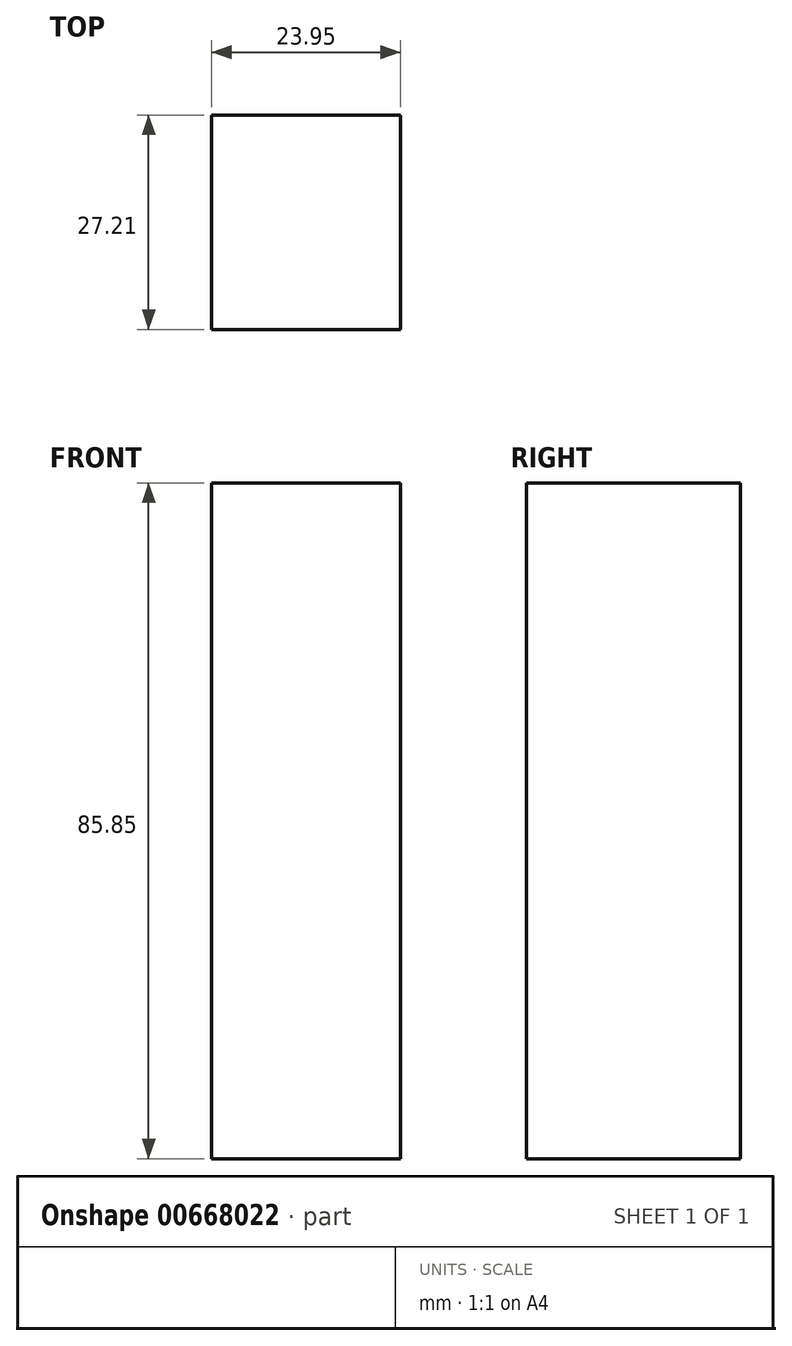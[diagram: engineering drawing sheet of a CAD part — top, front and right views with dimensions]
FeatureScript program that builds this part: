
annotation { "Feature Type Name" : "Feature", "Feature Type Description" : "" }
export const myFeature = defineFeature(function(context is Context, id is Id, definition is map)
    precondition{}
    {
        {
            var Q0;
            Q0=qCreatedBy(makeId("Top.planeOp"),FACE);
            var sketch = newSketch(context, id + "F0", { "sketchPlane" : qUnion([Q0])});
            skLineSegment(sketch, "E0.bottom", {"start": v(-65.47, 56.4) * mm, "end": v(-51.52, 56.4) * mm});
            skLineSegment(sketch, "E0.top", {"start": v(-65.47, -55.94) * mm, "end": v(-51.52, -55.94) * mm});
            skLineSegment(sketch, "E0.left", {"start": v(-65.47, 56.4) * mm, "end": v(-65.47, -55.94) * mm});
            skLineSegment(sketch, "E0.right", {"start": v(-51.52, 56.4) * mm, "end": v(-51.52, -55.94) * mm});
            skLineSegment(sketch, "E1.bottom", {"start": v(-51.52, -42.91) * mm, "end": v(49.42, -42.91) * mm});
            skLineSegment(sketch, "E1.top", {"start": v(-51.52, -55.94) * mm, "end": v(49.42, -55.94) * mm});
            skLineSegment(sketch, "E1.left", {"start": v(-51.52, -42.91) * mm, "end": v(-51.52, -55.94) * mm});
            skLineSegment(sketch, "E1.right", {"start": v(49.42, -42.91) * mm, "end": v(49.42, -55.94) * mm});
            skLineSegment(sketch, "E2.bottom", {"start": v(49.42, -42.91) * mm, "end": v(33.14, -42.91) * mm});
            skLineSegment(sketch, "E2.top", {"start": v(49.42, 55.94) * mm, "end": v(33.14, 55.94) * mm});
            skLineSegment(sketch, "E2.left", {"start": v(49.42, -42.91) * mm, "end": v(49.42, 55.94) * mm});
            skLineSegment(sketch, "E2.right", {"start": v(33.14, -42.91) * mm, "end": v(33.14, 55.94) * mm});
            skLineSegment(sketch, "E3.bottom", {"start": v(33.14, 55.94) * mm, "end": v(-51.52, 55.94) * mm});
            skLineSegment(sketch, "E3.top", {"start": v(33.14, 41.98) * mm, "end": v(-51.52, 41.98) * mm});
            skLineSegment(sketch, "E3.left", {"start": v(33.14, 55.94) * mm, "end": v(33.14, 41.98) * mm});
            skLineSegment(sketch, "E3.right", {"start": v(-51.52, 55.94) * mm, "end": v(-51.52, 41.98) * mm});
            skLineSegment(sketch, "E4.bottom", {"start": v(-44.54, 33.14) * mm, "end": v(-33.14, 33.14) * mm});
            skLineSegment(sketch, "E4.top", {"start": v(-44.54, -37.1) * mm, "end": v(-33.14, -37.1) * mm});
            skLineSegment(sketch, "E4.left", {"start": v(-44.54, 33.14) * mm, "end": v(-44.54, -37.1) * mm});
            skLineSegment(sketch, "E4.right", {"start": v(-33.14, 33.14) * mm, "end": v(-33.14, -37.1) * mm});
            skLineSegment(sketch, "E5.bottom", {"start": v(-33.14, 33.14) * mm, "end": v(25, 33.14) * mm});
            skLineSegment(sketch, "E5.top", {"start": v(-33.14, 24.54) * mm, "end": v(25, 24.54) * mm});
            skLineSegment(sketch, "E5.left", {"start": v(-33.14, 33.14) * mm, "end": v(-33.14, 24.54) * mm});
            skLineSegment(sketch, "E5.right", {"start": v(25, 33.14) * mm, "end": v(25, 24.54) * mm});
            skLineSegment(sketch, "E6.bottom", {"start": v(25, 24.54) * mm, "end": v(17.1, 24.54) * mm});
            skLineSegment(sketch, "E6.top", {"start": v(25, -37.1) * mm, "end": v(17.1, -37.1) * mm});
            skLineSegment(sketch, "E6.left", {"start": v(25, 24.54) * mm, "end": v(25, -37.1) * mm});
            skLineSegment(sketch, "E6.right", {"start": v(17.1, 24.54) * mm, "end": v(17.1, -37.1) * mm});
            skLineSegment(sketch, "E7.bottom", {"start": v(17.1, -29.89) * mm, "end": v(-33.14, -29.89) * mm});
            skLineSegment(sketch, "E7.top", {"start": v(17.1, -37.1) * mm, "end": v(-33.14, -37.1) * mm});
            skLineSegment(sketch, "E7.left", {"start": v(17.1, -29.89) * mm, "end": v(17.1, -37.1) * mm});
            skLineSegment(sketch, "E7.right", {"start": v(-33.14, -29.89) * mm, "end": v(-33.14, -37.1) * mm});
            skLineSegment(sketch, "E8.bottom", {"start": v(-22.21, 11.28) * mm, "end": v(-28.5, 11.28) * mm});
            skLineSegment(sketch, "E8.top", {"start": v(-22.21, -21.98) * mm, "end": v(-28.5, -21.98) * mm});
            skLineSegment(sketch, "E8.left", {"start": v(-22.21, 11.28) * mm, "end": v(-22.21, -21.98) * mm});
            skLineSegment(sketch, "E8.right", {"start": v(-28.5, 11.28) * mm, "end": v(-28.5, -21.98) * mm});
            skLineSegment(sketch, "E9.bottom", {"start": v(-22.21, -21.98) * mm, "end": v(9.42, -21.98) * mm});
            skLineSegment(sketch, "E9.top", {"start": v(-22.21, -15.93) * mm, "end": v(9.42, -15.93) * mm});
            skLineSegment(sketch, "E9.left", {"start": v(-22.21, -21.98) * mm, "end": v(-22.21, -15.93) * mm});
            skLineSegment(sketch, "E9.right", {"start": v(9.42, -21.98) * mm, "end": v(9.42, -15.93) * mm});
            skLineSegment(sketch, "E10.bottom", {"start": v(9.42, -15.93) * mm, "end": v(1.74, -15.93) * mm});
            skLineSegment(sketch, "E10.top", {"start": v(9.42, 11.28) * mm, "end": v(1.74, 11.28) * mm});
            skLineSegment(sketch, "E10.left", {"start": v(9.42, -15.93) * mm, "end": v(9.42, 11.28) * mm});
            skLineSegment(sketch, "E10.right", {"start": v(1.74, -15.93) * mm, "end": v(1.74, 11.28) * mm});
            skLineSegment(sketch, "E11.bottom", {"start": v(-22.21, 11.28) * mm, "end": v(1.74, 11.28) * mm});
            skLineSegment(sketch, "E11.top", {"start": v(-22.21, 3.37) * mm, "end": v(1.74, 3.37) * mm});
            skLineSegment(sketch, "E11.left", {"start": v(-22.21, 11.28) * mm, "end": v(-22.21, 3.37) * mm});
            skLineSegment(sketch, "E11.right", {"start": v(1.74, 11.28) * mm, "end": v(1.74, 3.37) * mm});
            skSolve(sketch);
        }
        {
            var Q0;
            Q0=makeQuery(id+"F0.imprint","IMPRINT",FACE,{"disambiguationData":[TD([[makeQuery(id+"F0.imprint","IMPRINT",EDGE,{"derivedFrom":sQuery(id+"F0.wireOp",EDGE,"E8.left")}),1.0]])]});
            var Q1;
            Q1=makeQuery(id+"F0.imprint","IMPRINT",FACE,{"disambiguationData":[TD([[makeQuery(id+"F0.imprint","IMPRINT",EDGE,{"derivedFrom":sQuery(id+"F0.wireOp",EDGE,"E10.bottom")}),-1.0]])]});
            extrude(context, id + "F1", {"entities" : qUnion([Q0, Q1]), "depth" : 85.85 * mm, "offsetDistance" : 25.4 * mm});
        }
    });
